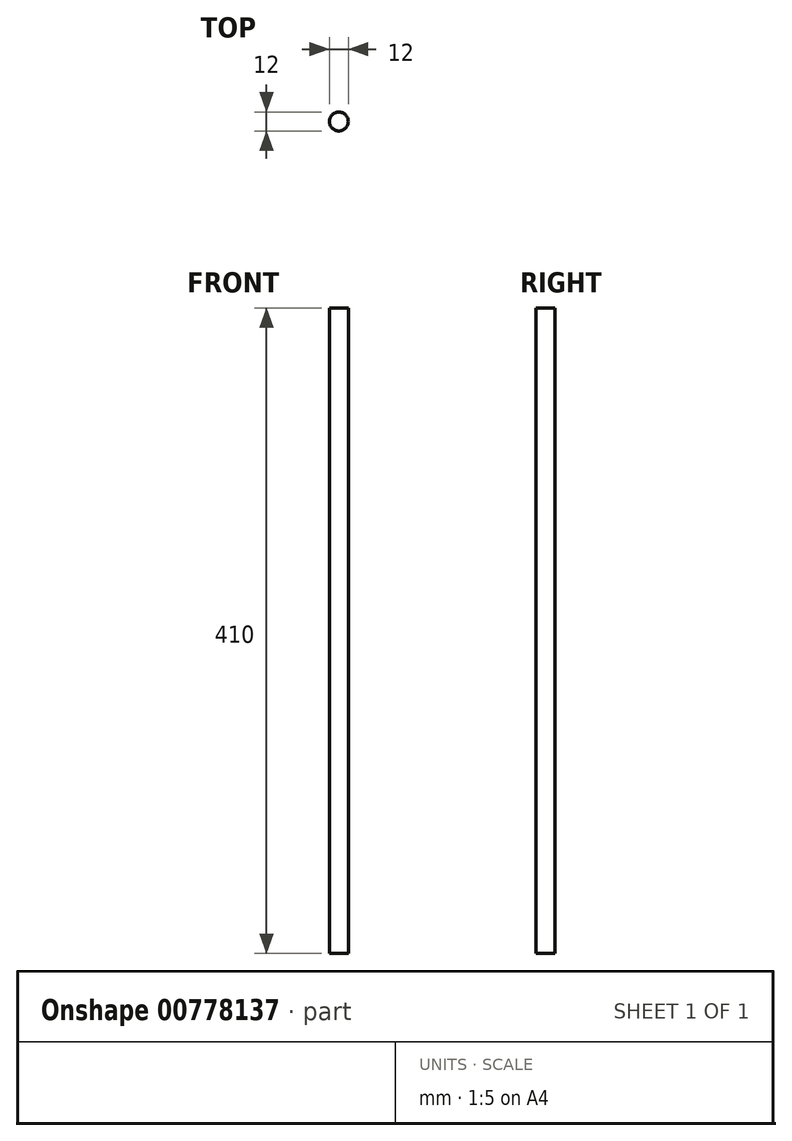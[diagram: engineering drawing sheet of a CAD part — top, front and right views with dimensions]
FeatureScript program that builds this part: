
annotation { "Feature Type Name" : "Feature", "Feature Type Description" : "" }
export const myFeature = defineFeature(function(context is Context, id is Id, definition is map)
    precondition{}
    {
        {
            assignVariable(context, id + "F0", {"name" : "length", "anyValue" : 410});
        }
        {
            var Q0;
            Q0=qCreatedBy(makeId("Top.planeOp"),FACE);
            var sketch = newSketch(context, id + "F1", { "sketchPlane" : qUnion([Q0])});
            skCircle(sketch, "E0", {"center": v(0, 0) * mm, "radius": 6 * mm});
            skSolve(sketch);
        }
        {
            var Q0;
            Q0 = qSketchRegion(id + "F1", true);
            extrude(context, id + "F2", {"entities" : qUnion([Q0]), "depth" : (getVariable(context, 'length')) * mm, "offsetDistance" : 25 * mm});
        }
    });
